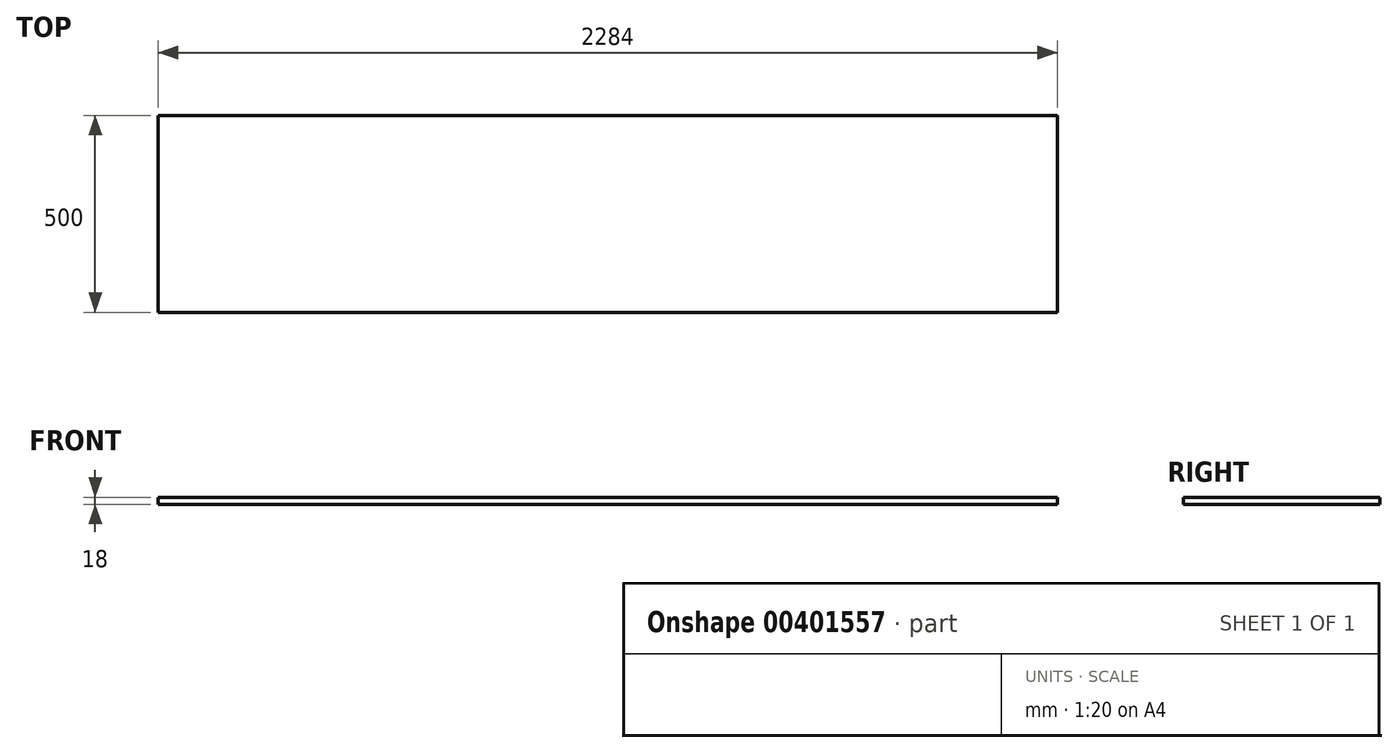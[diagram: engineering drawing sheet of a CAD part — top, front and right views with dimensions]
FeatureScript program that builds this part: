
annotation { "Feature Type Name" : "Feature", "Feature Type Description" : "" }
export const myFeature = defineFeature(function(context is Context, id is Id, definition is map)
    precondition{}
    {
        {
            var Q0;
            Q0=qCreatedBy(makeId("Top.planeOp"),FACE);
            var sketch = newSketch(context, id + "F0", { "sketchPlane" : qUnion([Q0])});
            skLineSegment(sketch, "E0.bottom", {"start": v(-1137.68, -398.05) * mm, "end": v(1146.32, -398.05) * mm});
            skLineSegment(sketch, "E0.top", {"start": v(-1137.68, -898.05) * mm, "end": v(1146.32, -898.05) * mm});
            skLineSegment(sketch, "E0.left", {"start": v(-1137.68, -398.05) * mm, "end": v(-1137.68, -898.05) * mm});
            skLineSegment(sketch, "E0.right", {"start": v(1146.32, -398.05) * mm, "end": v(1146.32, -898.05) * mm});
            skSolve(sketch);
        }
        {
            var Q0;
            Q0=makeQuery(id+"F0.imprint","IMPRINT",FACE,{"disambiguationData":[TD([[makeQuery(id+"F0.imprint","IMPRINT",EDGE,{"derivedFrom":sQuery(id+"F0.wireOp",EDGE,"E0.bottom")}),-1.0]])]});
            extrude(context, id + "F1", {"entities" : qUnion([Q0]), "depth" : 18 * mm});
        }
    });
